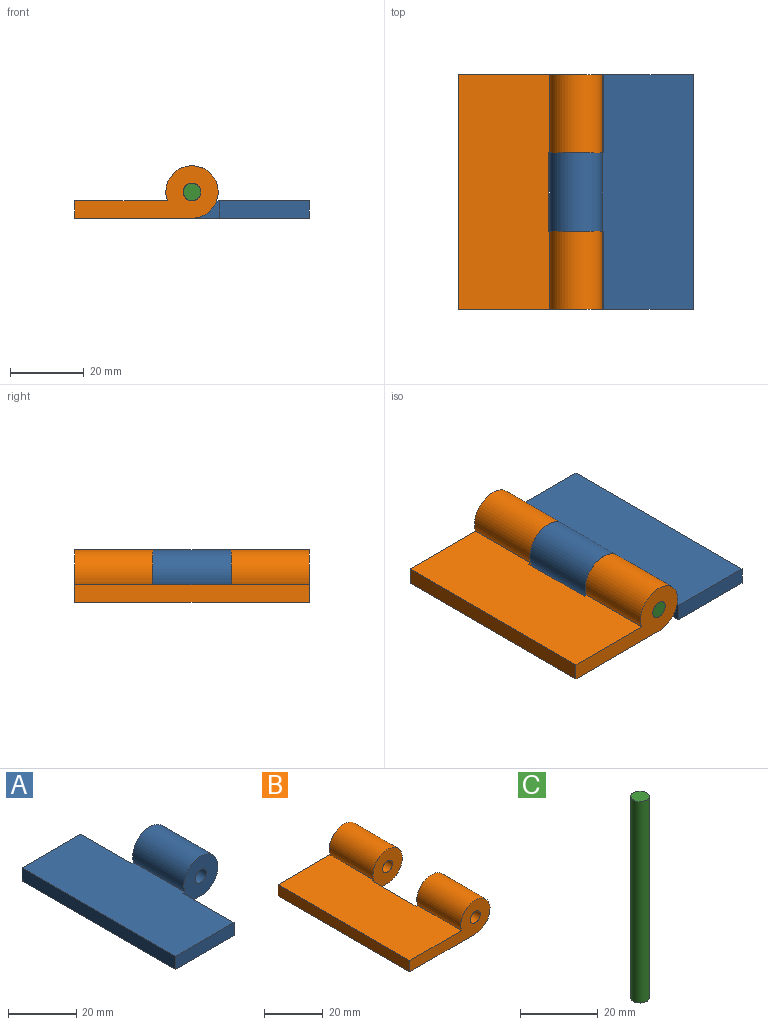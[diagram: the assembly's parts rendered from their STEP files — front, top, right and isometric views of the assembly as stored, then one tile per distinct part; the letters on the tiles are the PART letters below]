
ASSEMBLY  parts=3 mates=3
PART A: 11 faces, bbox 38.8x63.5x14.2 mm
  f0: plane 63.5x31.75mm, normal (0,0,-1), area 1700.1mm2, adj f1,f3,f4,f5,f6,f7,f8,f9
  f1: cylinder r=7.08mm len=21.17mm, axis (0,1,0), area 757.9mm2, adj f0,f2,f6,f8
  f2: plane 63.5x25.08mm, normal (0,0,1), area 1558.9mm2, adj f1,f3,f4,f5,f6,f7,f8,f9
  f3: plane 63.5x4.7mm, normal (-1,0,0), area 298.5mm2, adj f0,f2,f4,f5
  f4: plane 24.29x4.7mm, normal (0,-1,0), area 114.2mm2, adj f0,f2,f3,f9
  f5: plane 24.28x4.7mm, normal (0,1,0), area 114.2mm2, adj f0,f2,f3,f7
  f6: plane 14.55x14.17mm, normal (0,1,0), area 152mm2, adj f0,f1,f2,f7,f10
  f7: plane 21.17x4.7mm, normal (1,0,0), area 99.5mm2, adj f0,f2,f5,f6
  f8: plane 14.54x14.17mm, normal (0,-1,0), area 152mm2, adj f0,f1,f2,f9,f10
  f9: plane 21.17x4.7mm, normal (1,0,0), area 99.5mm2, adj f0,f2,f4,f8
  f10: cylinder r=2.38mm len=21.17mm, axis (0,1,0), area 316.7mm2, adj f6,f8
PART B: 12 faces, bbox 38.8x63.5x14.2 mm
  f0: cylinder r=7.08mm len=21.17mm, axis (0,1,0), area 757.9mm2, adj f2,f4,f7,f9
  f1: cylinder r=2.38mm len=21.17mm, axis (0,1,0), area 316.7mm2, adj f7,f9
  f2: plane 63.5x25.08mm, normal (0,0,1), area 1575.8mm2, adj f0,f3,f5,f7,f8,f9,f10,f11
  f3: plane 63.5x4.7mm, normal (-1,0,0), area 298.5mm2, adj f2,f4,f7,f8
  f4: plane 63.5x31.75mm, normal (0,0,-1), area 1858.2mm2, adj f0,f3,f5,f7,f8,f9,f10,f11
  f5: cylinder r=7.08mm len=21.17mm, axis (0,1,0), area 757.9mm2, adj f2,f4,f8,f10
  f6: cylinder r=2.38mm len=21.17mm, axis (0,1,0), area 316.7mm2, adj f8,f10
  f7: plane 38.83x14.17mm, normal (0,-1,0), area 266.2mm2, adj f0,f1,f2,f3,f4
  f8: plane 38.83x14.17mm, normal (0,1,0), area 266.2mm2, adj f2,f3,f4,f5,f6
  f9: plane 14.54x14.17mm, normal (0,1,0), area 152mm2, adj f0,f1,f2,f4,f11
  f10: plane 14.54x14.17mm, normal (0,-1,0), area 152mm2, adj f2,f4,f5,f6,f11
  f11: plane 21.17x4.7mm, normal (1,0,0), area 99.5mm2, adj f2,f4,f9,f10
PART C: 3 faces, bbox 4.8x4.8x63.5 mm
  f0: cylinder r=2.38mm len=63.5mm, axis (0,0,-1), area 950.1mm2, adj f1,f2
  f1: plane 4.76x4.76mm, normal (0,0,1), area 17.8mm2, adj f0
  f2: plane 4.76x4.76mm, normal (0,0,-1), area 17.8mm2, adj f0
PLACE A rot(axis=(0,0,1),180deg) t=(-66.73,-52.55,-36.04)mm
PLACE B t=(-49.17,10.95,-19.66)mm fixed
PLACE C rot(axis=(-1,0,0),90deg) t=(-17.42,-52.55,-12.58)mm
MATE revolute A.f1 <-> B.f0  axis (0,-1,0) through (-17.42,-31.39,-12.58)mm
MATE planar C.f0 <-> B.f0  axis (0,-1,0) through (-17.42,-52.55,-12.58)mm
MATE ball A.f1 <-> C.f0  axis (0,-1,0) through (-17.42,-20.8,-12.58)mm
